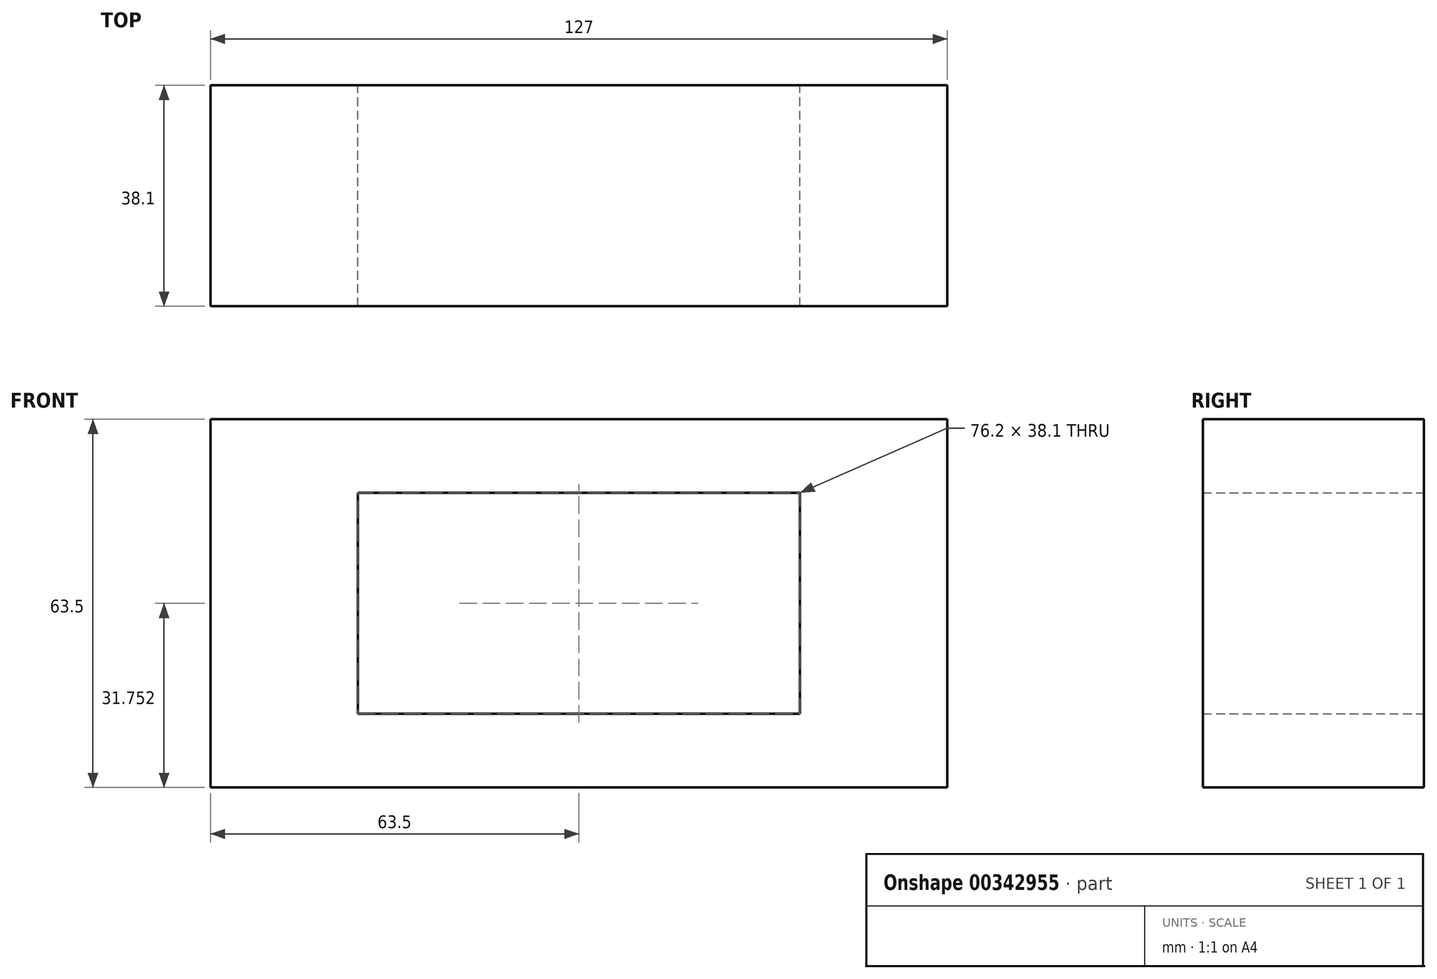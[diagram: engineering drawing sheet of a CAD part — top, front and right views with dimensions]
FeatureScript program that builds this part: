
annotation { "Feature Type Name" : "Feature", "Feature Type Description" : "" }
export const myFeature = defineFeature(function(context is Context, id is Id, definition is map)
    precondition{}
    {
        {
            var Q0;
            Q0=qCreatedBy(makeId("Front.planeOp"),FACE);
            var sketch = newSketch(context, id + "F0", { "sketchPlane" : qUnion([Q0])});
            skLineSegment(sketch, "E0", {"start": v(-53.59, -39.08) * mm, "end": v(73.41, -39.08) * mm});
            skLineSegment(sketch, "E1", {"start": v(-53.59, -39.08) * mm, "end": v(-53.59, 24.42) * mm});
            skLineSegment(sketch, "E2", {"start": v(-53.59, 24.42) * mm, "end": v(73.41, 24.42) * mm});
            skLineSegment(sketch, "E3", {"start": v(73.41, 24.42) * mm, "end": v(73.41, -39.08) * mm});
            skLineSegment(sketch, "E4.top", {"start": v(-53.59, 24.42) * mm, "end": v(-28.19, 24.42) * mm});
            skLineSegment(sketch, "E4.left", {"start": v(-53.59, 11.72) * mm, "end": v(-53.59, 24.42) * mm});
            skLineSegment(sketch, "E5.top", {"start": v(-53.59, -39.08) * mm, "end": v(-28.19, -39.08) * mm});
            skLineSegment(sketch, "E5.left", {"start": v(-53.59, -26.38) * mm, "end": v(-53.59, -39.08) * mm});
            skLineSegment(sketch, "E6.bottom", {"start": v(48.01, 24.42) * mm, "end": v(73.41, 24.42) * mm});
            skLineSegment(sketch, "E6.right", {"start": v(73.41, 24.42) * mm, "end": v(73.41, 11.72) * mm});
            skLineSegment(sketch, "E7.bottom", {"start": v(73.41, -39.08) * mm, "end": v(48.01, -39.08) * mm});
            skLineSegment(sketch, "E7.left", {"start": v(73.41, -39.08) * mm, "end": v(73.41, -26.38) * mm});
            skLineSegment(sketch, "E8", {"start": v(-28.19, 11.72) * mm, "end": v(-28.19, -26.38) * mm});
            skLineSegment(sketch, "E9", {"start": v(-28.19, -26.38) * mm, "end": v(48.01, -26.38) * mm});
            skLineSegment(sketch, "E10", {"start": v(48.01, 11.72) * mm, "end": v(48.01, -26.38) * mm});
            skLineSegment(sketch, "E11", {"start": v(48.01, 11.72) * mm, "end": v(-28.19, 11.72) * mm});
            skSolve(sketch);
        }
        {
            var Q0;
            Q0=makeQuery(id+"F0.imprint","IMPRINT",FACE,{"disambiguationData":[TD([[makeQuery(id+"F0.imprint","IMPRINT",EDGE,{"derivedFrom":sQuery(id+"F0.wireOp",EDGE,"E0")}),1.0]])]});
            extrude(context, id + "F1", {"entities" : qUnion([Q0]), "depth" : 38.1 * mm});
        }
    });
